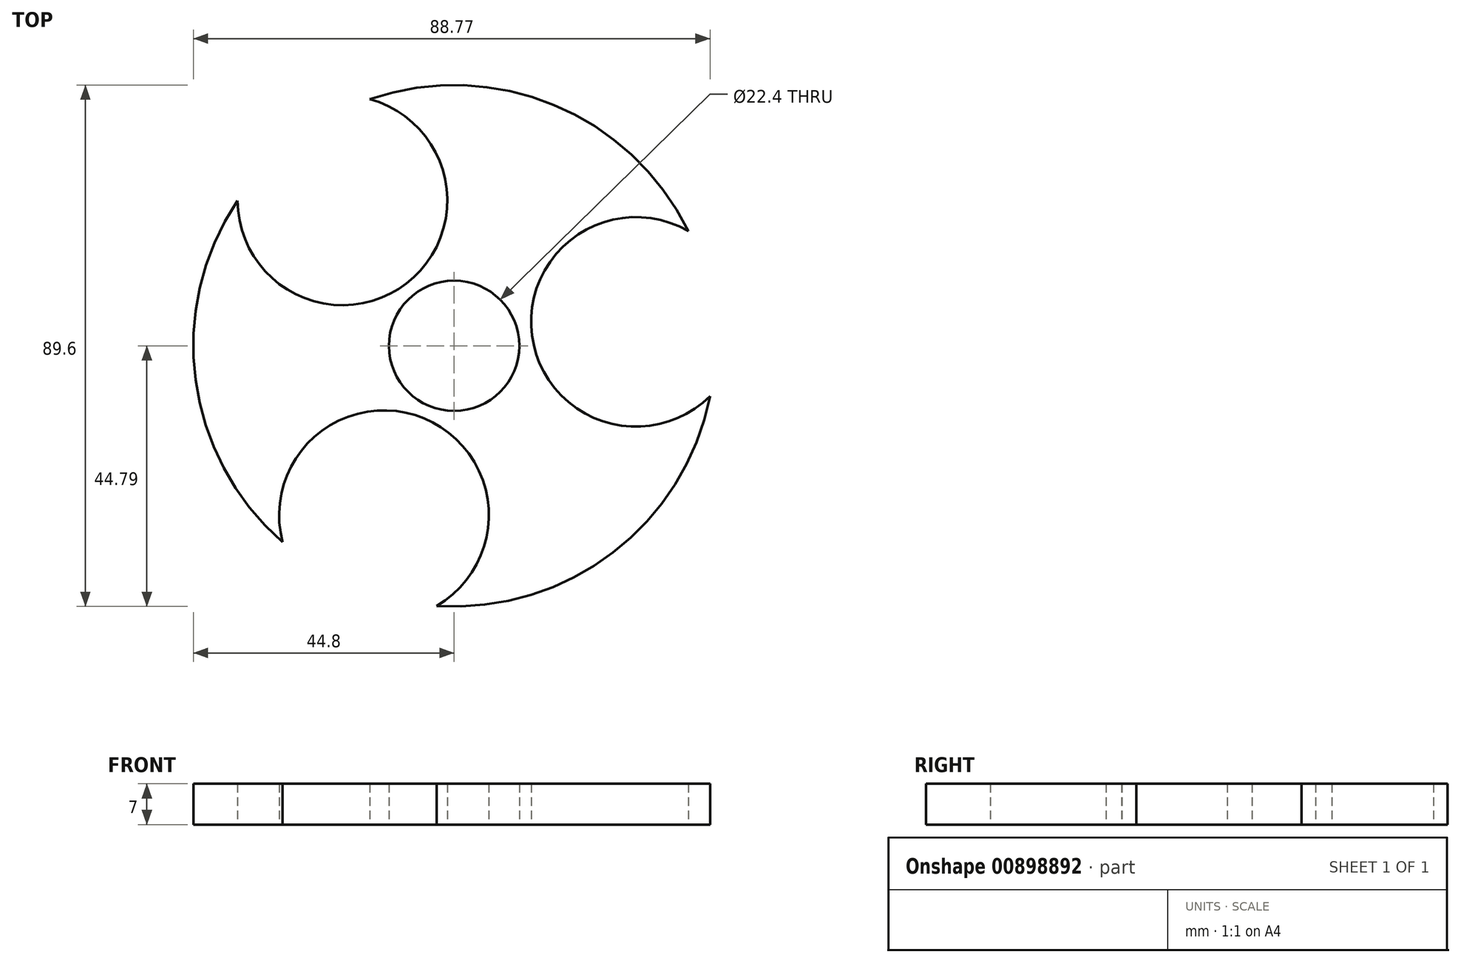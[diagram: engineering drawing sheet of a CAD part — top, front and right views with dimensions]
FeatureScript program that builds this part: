
annotation { "Feature Type Name" : "Feature", "Feature Type Description" : "" }
export const myFeature = defineFeature(function(context is Context, id is Id, definition is map)
    precondition{}
    {
        {
            var Q0;
            Q0=qCreatedBy(makeId("Top.planeOp"),FACE);
            var sketch = newSketch(context, id + "F0", { "sketchPlane" : qUnion([Q0])});
            skCircle(sketch, "E0", {"center": v(0, 0) * mm, "radius": 11.2 * mm});
            skArc(sketch, "E1", {"start": v(40.21, 19.73) * mm, "mid": v(17.13, 41.4) * mm, "end": v(-14.51, 42.4) * mm});
            skArc(sketch, "E2.1.0", {"start": v(-37.2, 24.96) * mm, "mid": v(-44.42, -5.87) * mm, "end": v(-29.46, -33.77) * mm});
            skArc(sketch, "E2.2.0", {"start": v(-3.02, -44.7) * mm, "mid": v(27.29, -35.53) * mm, "end": v(43.97, -8.63) * mm});
            skArc(sketch, "E3", {"start": v(-37.2, 24.96) * mm, "mid": v(-8.2, 10.72) * mm, "end": v(-14.51, 42.4) * mm});
            skArc(sketch, "E4.1.0", {"start": v(-3.02, -44.7) * mm, "mid": v(-5.18, -12.47) * mm, "end": v(-29.46, -33.77) * mm});
            skArc(sketch, "E4.2.0", {"start": v(40.21, 19.73) * mm, "mid": v(13.39, 1.75) * mm, "end": v(43.97, -8.63) * mm});
            skSolve(sketch);
        }
        {
            var Q0;
            Q0 = qSketchRegion(id + "F0", true);
            extrude(context, id + "F1", {"entities" : qUnion([Q0]), "depth" : 7 * mm, "offsetDistance" : 25 * mm});
        }
    });
